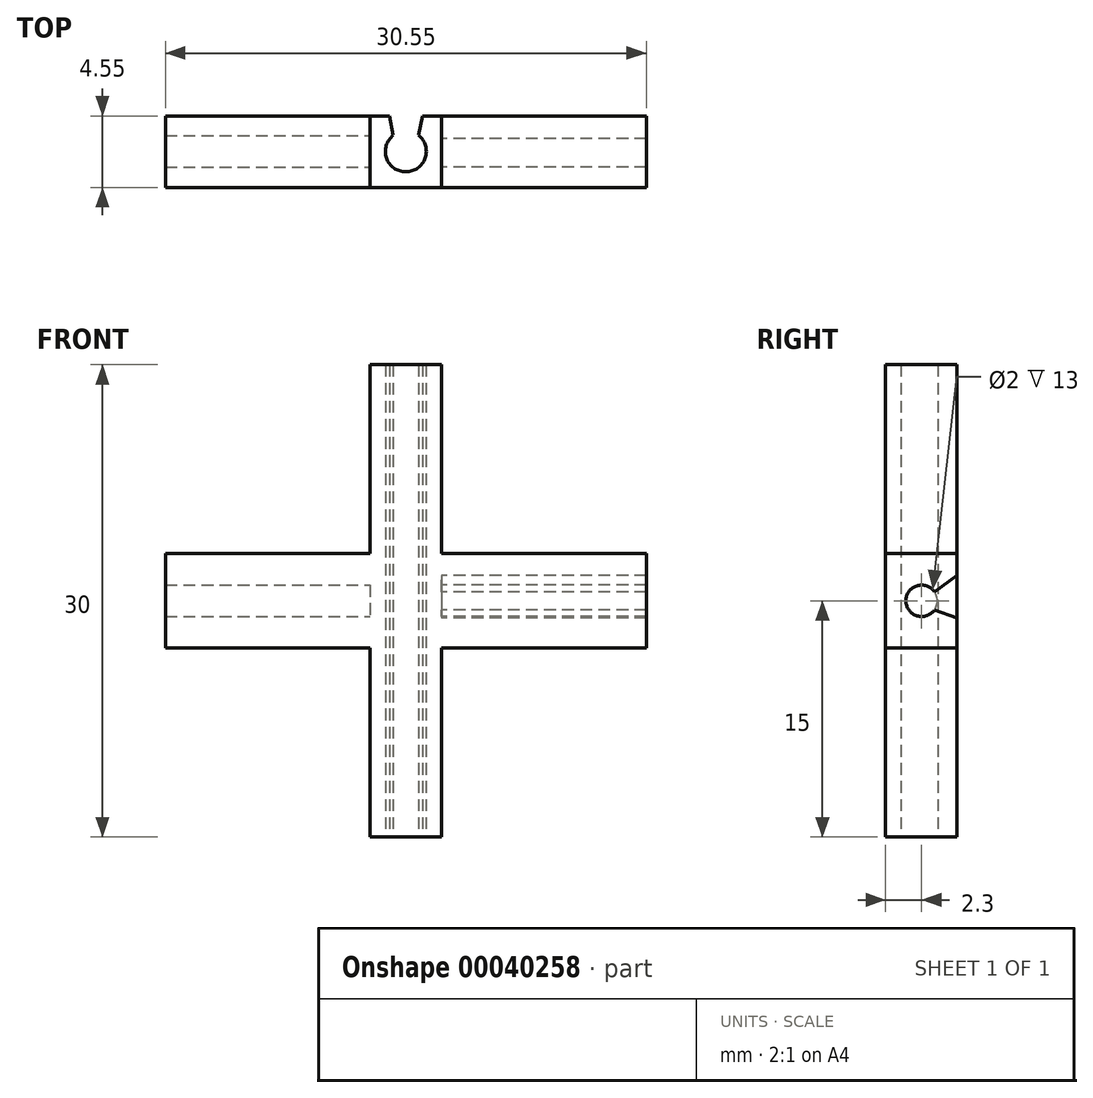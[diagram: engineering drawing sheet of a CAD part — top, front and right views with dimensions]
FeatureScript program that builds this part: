
annotation { "Feature Type Name" : "Feature", "Feature Type Description" : "" }
export const myFeature = defineFeature(function(context is Context, id is Id, definition is map)
    precondition{}
    {
        {
            var Q0;
            Q0=qCreatedBy(makeId("Top.planeOp"),FACE);
            var sketch = newSketch(context, id + "F0", { "sketchPlane" : qUnion([Q0])});
            skCircle(sketch, "E0", {"center": v(0, 0) * mm, "radius": 1.3 * mm});
            skCircle(sketch, "E1", {"center": v(0, 0) * mm, "radius": 2.25 * mm});
            skLineSegment(sketch, "E2", {"start": v(0, 1.3) * mm, "end": v(0, 2.25) * mm, "construction": true});
            skLineSegment(sketch, "E3", {"start": v(-0.8, 1.02) * mm, "end": v(-1, 2.02) * mm, "construction": true});
            skLineSegment(sketch, "E4", {"start": v(0.8, 1.02) * mm, "end": v(1, 2.02) * mm, "construction": true});
            skLineSegment(sketch, "E5", {"start": v(-0.8, 1.02) * mm, "end": v(-1, 2.02) * mm});
            skLineSegment(sketch, "E6", {"start": v(0.8, 1.02) * mm, "end": v(1, 2.02) * mm});
            skLineSegment(sketch, "E7.bottom", {"start": v(-2.27, 2.25) * mm, "end": v(2.28, 2.25) * mm});
            skLineSegment(sketch, "E7.top", {"start": v(-2.27, -2.3) * mm, "end": v(2.28, -2.3) * mm});
            skLineSegment(sketch, "E7.left", {"start": v(-2.27, 2.25) * mm, "end": v(-2.27, -2.3) * mm});
            skLineSegment(sketch, "E7.right", {"start": v(2.28, 2.25) * mm, "end": v(2.28, -2.3) * mm});
            skLineSegment(sketch, "E8", {"start": v(-1, 2.02) * mm, "end": v(-1.05, 2.25) * mm});
            skLineSegment(sketch, "E9", {"start": v(1, 2.02) * mm, "end": v(1.05, 2.25) * mm});
            skSolve(sketch);
        }
        {
            var Q0;
            {var subQ1=sQuery(id+"F0.wireOp",EDGE,"E5");Q0=makeQuery(id+"F0.imprint","IMPRINT",FACE,{"disambiguationData":[TD([[makeQuery(id+"F0.imprint","IMPRINT",EDGE,{"derivedFrom":subQ1}),1.0]])]});}
            var Q1;
            Q1=makeQuery(id+"F0.imprint","IMPRINT",FACE,{"disambiguationData":[TD([[makeQuery(id+"F0.imprint","IMPRINT",EDGE,{"derivedFrom":sQuery(id+"F0.wireOp",EDGE,"E7.top")}),1.0]])]});
            extrude(context, id + "F1", {"entities" : qUnion([Q0, Q1]), "depth" : 30 * mm});
        }
        {
            var Q0;
            Q0=makeQuery(id+"F1.opExtrude","SWEPT_FACE",FACE,{"disambiguationData":[OSD([sQuery(id+"F0.wireOp",EDGE,"E7.right")])]});
            var sketch = newSketch(context, id + "F2", { "sketchPlane" : qUnion([Q0])});
            skCircle(sketch, "E10", {"center": v(0, 15) * mm, "radius": 1 * mm});
            skPoint(sketch, "E10.centerSnap0", {"position": v(2.25, 15) * mm});
            skLineSegment(sketch, "E11", {"start": v(2.25, 18) * mm, "end": v(-2.3, 18) * mm});
            skLineSegment(sketch, "E12", {"start": v(-2.3, 12) * mm, "end": v(2.25, 12) * mm});
            skLineSegment(sketch, "E13", {"start": v(1, 15) * mm, "end": v(2.25, 15) * mm, "construction": true});
            skLineSegment(sketch, "E14", {"start": v(0.82, 15.57) * mm, "end": v(2.25, 16.62) * mm, "construction": true});
            skLineSegment(sketch, "E15", {"start": v(0.82, 14.43) * mm, "end": v(2.25, 13.91) * mm, "construction": true});
            skLineSegment(sketch, "E16", {"start": v(0.82, 15.57) * mm, "end": v(2.25, 16.62) * mm});
            skLineSegment(sketch, "E17", {"start": v(0.82, 14.43) * mm, "end": v(2.25, 13.91) * mm});
            skSolve(sketch);
        }
        {
            var Q0;
            {var subQ3=sQuery(id+"F2.wireOp",EDGE,"E11");Q0=makeQuery(id+"F2.imprint","IMPRINT",FACE,{"disambiguationData":[TD([[makeQuery(id+"F2.imprint","IMPRINT",EDGE,{"derivedFrom":subQ3}),1.0]])]});}
            extrude(context, id + "F3", {"entities" : qUnion([Q0]), "operationType" : NewBodyOperationType.ADD, "depth" : 13 * mm});
        }
        {
            var Q0;
            Q0=makeQuery(id+"F1.opExtrude","SWEPT_FACE",FACE,{"disambiguationData":[OSD([sQuery(id+"F0.wireOp",EDGE,"E7.left")])]});
            var sketch = newSketch(context, id + "F4", { "sketchPlane" : qUnion([Q0])});
            skCircle(sketch, "E18", {"center": v(0, 15) * mm, "radius": 1 * mm});
            skPoint(sketch, "E18.centerSnap0", {"position": v(-2.25, 15) * mm});
            skLineSegment(sketch, "E19", {"start": v(-2.25, 18) * mm, "end": v(2.3, 18) * mm});
            skLineSegment(sketch, "E20", {"start": v(2.3, 12) * mm, "end": v(-2.25, 12) * mm});
            skSolve(sketch);
        }
        {
            var Q0;
            Q0=makeQuery(id+"F4.imprint","IMPRINT",FACE,{"disambiguationData":[TD([[makeQuery(id+"F4.imprint","IMPRINT",EDGE,{"derivedFrom":sQuery(id+"F4.wireOp",EDGE,"E18")}),-1.0]])]});
            extrude(context, id + "F5", {"entities" : qUnion([Q0]), "operationType" : NewBodyOperationType.ADD, "depth" : 13 * mm});
        }
    });
